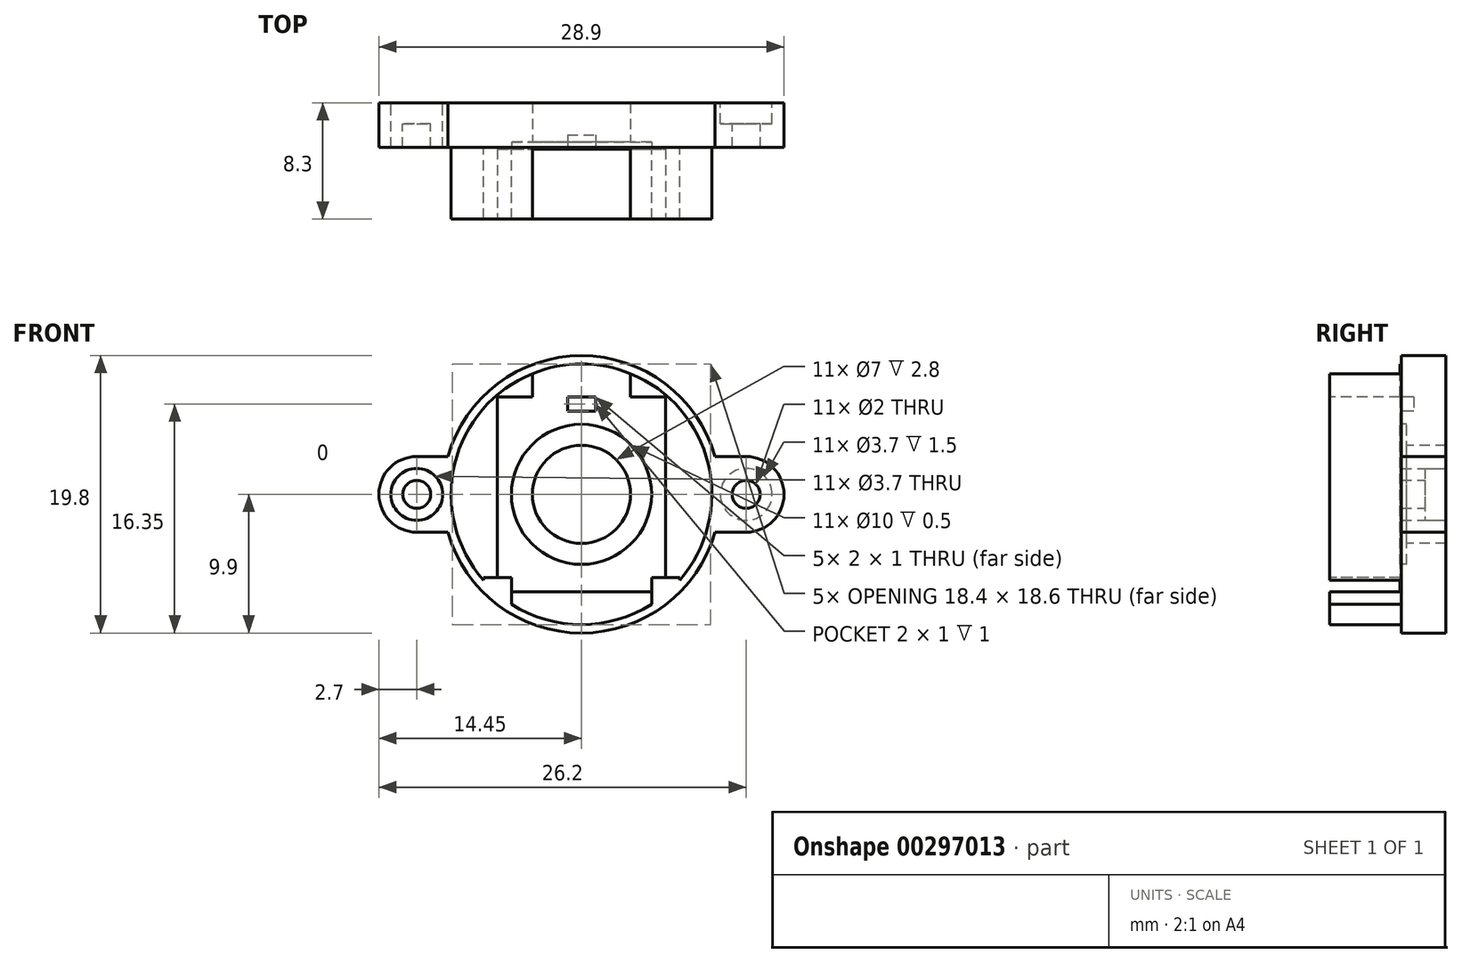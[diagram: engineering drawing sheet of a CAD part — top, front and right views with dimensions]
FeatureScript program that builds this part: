
annotation { "Feature Type Name" : "Feature", "Feature Type Description" : "" }
export const myFeature = defineFeature(function(context is Context, id is Id, definition is map)
    precondition{}
    {
        {
            var Q0;
            Q0=qCreatedBy(makeId("Top.planeOp"),FACE);
            var sketch = newSketch(context, id + "F0", { "sketchPlane" : qUnion([Q0])});
            skLineSegment(sketch, "E0", {"start": v(0, -5.1) * mm, "end": v(-9.3, -5.1) * mm});
            skLineSegment(sketch, "E1", {"start": v(-9.3, -5.1) * mm, "end": v(-9.3, 0) * mm});
            skLineSegment(sketch, "E2", {"start": v(-9.3, 0) * mm, "end": v(-9.9, 0) * mm});
            skLineSegment(sketch, "E3", {"start": v(-9.9, 0) * mm, "end": v(-9.9, 3.2) * mm});
            skLineSegment(sketch, "E4", {"start": v(-9.9, 3.2) * mm, "end": v(0, 3.2) * mm});
            skLineSegment(sketch, "E5", {"start": v(0, 3.2) * mm, "end": v(0, -5.1) * mm});
            skSolve(sketch);
        }
        {
            var Q0;
            Q0=makeQuery(id+"F0.imprint","IMPRINT",FACE,{"disambiguationData":[TD([[makeQuery(id+"F0.imprint","IMPRINT",EDGE,{"derivedFrom":sQuery(id+"F0.wireOp",EDGE,"E0")}),-1.0]])]});
            var Q1;
            Q1=sQuery(id+"F0.wireOp",EDGE,"E5");
            revolve(context, id + "F1", {"entities" : qUnion([Q0]), "axis" : qUnion([Q1]), "revolveType" : RevolveType.FULL});
        }
        {
            var Q0;
            Q0=makeQuery(id+"F1.opRevolve","SWEPT_FACE",FACE,{"disambiguationData":[OSD([sQuery(id+"F0.wireOp",EDGE,"E4")])]});
            var sketch = newSketch(context, id + "F2", { "sketchPlane" : qUnion([Q0])});
            skLineSegment(sketch, "E6", {"start": v(9.52, -2.7) * mm, "end": v(11.75, -2.7) * mm});
            skArc(sketch, "E7", {"start": v(11.75, -2.7) * mm, "mid": v(13.66, -1.9) * mm, "end": v(14.45, 0) * mm});
            skPoint(sketch, "E8", {"position": v(14.45, 0) * mm});
            skPoint(sketch, "E8.positionSnap0", {"position": v(14.45, 0) * mm});
            skPoint(sketch, "E9", {"position": v(9.9, 0) * mm});
            skLineSegment(sketch, "E10", {"start": v(0, -2.12) * mm, "end": v(0, 2.3) * mm, "construction": true});
            skLineSegment(sketch, "E11.MirrorCS", {"start": v(-9.52, -2.7) * mm, "end": v(-11.75, -2.7) * mm});
            skArc(sketch, "E12.MirrorCS", {"start": v(-11.75, -2.7) * mm, "mid": v(-13.66, -1.9) * mm, "end": v(-14.45, 0) * mm});
            skPoint(sketch, "E13.MirrorP", {"position": v(-14.45, 0) * mm});
            skPoint(sketch, "E14.end.orphan", {"position": v(9.52, 2.7) * mm});
            skPoint(sketch, "E14.start.orphan", {"position": v(11.75, 2.7) * mm});
            skPoint(sketch, "E15.MirrorCS.end.orphan", {"position": v(-9.52, 2.7) * mm});
            skPoint(sketch, "E15.MirrorCS.start.orphan", {"position": v(-11.75, 2.7) * mm});
            skLineSegment(sketch, "E16", {"start": v(2.14, 0) * mm, "end": v(-2.79, 0) * mm, "construction": true});
            skArc(sketch, "E17.MirrorCS", {"start": v(11.75, 2.7) * mm, "mid": v(13.66, 1.9) * mm, "end": v(14.45, 0) * mm});
            skLineSegment(sketch, "E18.MirrorCS", {"start": v(9.52, 2.7) * mm, "end": v(11.75, 2.7) * mm});
            skLineSegment(sketch, "E19.MirrorCS", {"start": v(-9.52, 2.7) * mm, "end": v(-11.75, 2.7) * mm});
            skArc(sketch, "E20.MirrorCS", {"start": v(-11.75, 2.7) * mm, "mid": v(-13.66, 1.9) * mm, "end": v(-14.45, 0) * mm});
            skPoint(sketch, "E21", {"position": v(-9.9, 0) * mm});
            skArc(sketch, "E22", {"start": v(9.52, -2.7) * mm, "mid": v(9.9, 0) * mm, "end": v(9.52, 2.7) * mm});
            skArc(sketch, "E23.MirrorCS", {"start": v(-9.52, -2.7) * mm, "mid": v(-9.9, 0) * mm, "end": v(-9.52, 2.7) * mm});
            skCircle(sketch, "E24", {"center": v(-11.75, 0) * mm, "radius": 1 * mm});
            skCircle(sketch, "E25.MirrorC", {"center": v(11.75, 0) * mm, "radius": 1 * mm});
            skPoint(sketch, "E26", {"position": v(10.75, 0) * mm});
            skPoint(sketch, "E27", {"position": v(-10.75, 0) * mm});
            skCircle(sketch, "E28", {"center": v(11.75, 0) * mm, "radius": 1.85 * mm});
            skCircle(sketch, "E29.MirrorC", {"center": v(-11.75, 0) * mm, "radius": 1.85 * mm});
            skSolve(sketch);
        }
        {
            var Q0;
            Q0=makeQuery(id+"F2.imprint","IMPRINT",FACE,{"disambiguationData":[TD([[makeQuery(id+"F2.imprint","IMPRINT",EDGE,{"derivedFrom":sQuery(id+"F2.wireOp",EDGE,"E11.MirrorCS")}),-1.0]])]});
            var Q1;
            Q1=makeQuery(id+"F2.imprint","IMPRINT",FACE,{"disambiguationData":[TD([[makeQuery(id+"F2.imprint","IMPRINT",EDGE,{"derivedFrom":sQuery(id+"F2.wireOp",EDGE,"E11.MirrorCS")}),-1.0]])]});
            var Q2;
            Q2=makeQuery(id+"F2.imprint","IMPRINT",FACE,{"disambiguationData":[TD([[makeQuery(id+"F2.imprint","IMPRINT",EDGE,{"derivedFrom":sQuery(id+"F2.wireOp",EDGE,"E11.MirrorCS")}),-1.0]])]});
            var Q3;
            Q3=makeQuery(id+"F2.imprint","IMPRINT",FACE,{"disambiguationData":[TD([[makeQuery(id+"F2.imprint","IMPRINT",EDGE,{"derivedFrom":sQuery(id+"F2.wireOp",EDGE,"E24")}),-1.0]])]});
            extrude(context, id + "F3", {"entities" : qUnion([Q0, Q1, Q2, Q3]), "oppositeDirection" : true, "depth" : 3.2 * mm});
        }
        {
            var Q0;
            Q0=makeQuery(id+"F1.opRevolve","SWEPT_FACE",FACE,{"disambiguationData":[OSD([sQuery(id+"F0.wireOp",EDGE,"E0")])]});
            var sketch = newSketch(context, id + "F4", { "sketchPlane" : qUnion([Q0])});
            skLineSegment(sketch, "E30.bottom", {"start": v(-6, 6.95) * mm, "end": v(6, 6.95) * mm});
            skLineSegment(sketch, "E30.top", {"start": v(-6, -6.95) * mm, "end": v(6, -6.95) * mm});
            skLineSegment(sketch, "E30.left", {"start": v(-6, 6.95) * mm, "end": v(-6, -6.95) * mm});
            skLineSegment(sketch, "E30.right", {"start": v(6, 6.95) * mm, "end": v(6, -6.95) * mm});
            skPoint(sketch, "E30.middle", {"position": v(0, 0) * mm});
            skSolve(sketch);
        }
        {
            var Q0;
            Q0 = qSketchRegion(id + "F4", true);
            extrude(context, id + "F5", {"entities" : qUnion([Q0]), "operationType" : NewBodyOperationType.REMOVE, "oppositeDirection" : true, "depth" : 5 * mm});
        }
        {
            var Q0;
            Q0=sQuery(id+"F4.wireOp",VERTEX,"E30.middle");
            var Q1;
            Q1=makeQuery(id+"F1.opRevolve","SWEPT_BODY",BODY,{"disambiguationData":[OSD([sQuery(id+"F0.wireOp",EDGE,"E0"),sQuery(id+"F0.wireOp",EDGE,"E1"),sQuery(id+"F0.wireOp",EDGE,"E2"),sQuery(id+"F0.wireOp",EDGE,"E3"),sQuery(id+"F0.wireOp",EDGE,"E4"),sQuery(id+"F0.wireOp",EDGE,"E5")])]});
            hole(context, id + "F6", {"style" : HoleStyle.SIMPLE, "endStyle" : HoleEndStyle.THROUGH, "holeDiameter" : 7 * mm, "tappedDepth" : 12 * mm, "tapClearance" : 3, "locations" : qUnion([Q0]), "scope" : qUnion([Q1])});
        }
        {
            var Q0;
            Q0=makeQuery(id+"F4.imprint","IMPRINT",FACE,{"disambiguationData":[TD([[makeQuery(id+"F4.imprint","IMPRINT",EDGE,{"derivedFrom":sQuery(id+"F4.wireOp",EDGE,"E30.bottom")}),1.0]])]});
            var sketch = newSketch(context, id + "F7", { "sketchPlane" : qUnion([Q0])});
            skLineSegment(sketch, "E31.bottom", {"start": v(1, 6.95) * mm, "end": v(-1, 6.95) * mm});
            skLineSegment(sketch, "E31.top", {"start": v(1, 5.95) * mm, "end": v(-1, 5.95) * mm});
            skLineSegment(sketch, "E31.left", {"start": v(1, 6.95) * mm, "end": v(1, 5.95) * mm});
            skLineSegment(sketch, "E31.right", {"start": v(-1, 6.95) * mm, "end": v(-1, 5.95) * mm});
            skPoint(sketch, "E32", {"position": v(0, 6.95) * mm});
            skSolve(sketch);
        }
        {
            var Q0;
            Q0 = qSketchRegion(id + "F7", true);
            extrude(context, id + "F8", {"entities" : qUnion([Q0]), "operationType" : NewBodyOperationType.REMOVE, "oppositeDirection" : true, "depth" : 6 * mm});
        }
        {
            var Q0;
            Q0=makeQuery(id+"F4.imprint","IMPRINT",FACE,{"disambiguationData":[TD([[makeQuery(id+"F4.imprint","IMPRINT",EDGE,{"derivedFrom":sQuery(id+"F4.wireOp",EDGE,"E30.bottom")}),1.0]])]});
            var sketch = newSketch(context, id + "F9", { "sketchPlane" : qUnion([Q0])});
            skLineSegment(sketch, "E33.bottom", {"start": v(-3.5, 6.95) * mm, "end": v(3.5, 6.95) * mm});
            skLineSegment(sketch, "E33.top", {"start": v(-3.5, 16.95) * mm, "end": v(3.5, 16.95) * mm});
            skLineSegment(sketch, "E33.left", {"start": v(-3.5, 6.95) * mm, "end": v(-3.5, 16.95) * mm});
            skLineSegment(sketch, "E33.right", {"start": v(3.5, 6.95) * mm, "end": v(3.5, 16.95) * mm});
            skPoint(sketch, "E34", {"position": v(0, 6.95) * mm});
            skSolve(sketch);
        }
        {
            var Q0;
            Q0 = qSketchRegion(id + "F9", true);
            extrude(context, id + "F10", {"entities" : qUnion([Q0]), "operationType" : NewBodyOperationType.REMOVE, "oppositeDirection" : true, "depth" : 5 * mm});
        }
        {
            var Q0;
            {var subQ1=sQuery(id+"F2.wireOp",EDGE,"E6");Q0=makeQuery(id+"F2.imprint","IMPRINT",FACE,{"disambiguationData":[TD([[makeQuery(id+"F2.imprint","IMPRINT",EDGE,{"derivedFrom":subQ1}),1.0]])]});}
            var Q1;
            Q1=makeQuery(id+"F2.imprint","IMPRINT",FACE,{"disambiguationData":[TD([[makeQuery(id+"F2.imprint","IMPRINT",EDGE,{"derivedFrom":sQuery(id+"F2.wireOp",EDGE,"E25.MirrorC")}),1.0]])]});
            var Q2;
            Q2=makeQuery(id+"F2.imprint","IMPRINT",FACE,{"disambiguationData":[TD([[makeQuery(id+"F2.imprint","IMPRINT",EDGE,{"derivedFrom":sQuery(id+"F2.wireOp",EDGE,"E25.MirrorC")}),-1.0]])]});
            extrude(context, id + "F11", {"entities" : qUnion([Q0, Q1, Q2]), "oppositeDirection" : true, "depth" : 3.2 * mm});
        }
        {
            var Q0;
            Q0=makeQuery(id+"F3.opExtrude","SWEPT_BODY",BODY,{"disambiguationData":[OSD([sQuery(id+"F2.wireOp",EDGE,"E11.MirrorCS"),sQuery(id+"F2.wireOp",EDGE,"E12.MirrorCS"),sQuery(id+"F2.wireOp",EDGE,"E19.MirrorCS"),sQuery(id+"F2.wireOp",EDGE,"E20.MirrorCS"),sQuery(id+"F2.wireOp",EDGE,"E23.MirrorCS")])]});
            var Q1;
            Q1=makeQuery(id+"F11.opExtrude","SWEPT_BODY",BODY,{"disambiguationData":[OSD([sQuery(id+"F2.wireOp",EDGE,"E6"),sQuery(id+"F2.wireOp",EDGE,"E7"),sQuery(id+"F2.wireOp",EDGE,"E17.MirrorCS"),sQuery(id+"F2.wireOp",EDGE,"E18.MirrorCS"),sQuery(id+"F2.wireOp",EDGE,"E22")])]});
            var Q2;
            Q2=makeQuery(id+"F1.opRevolve","SWEPT_BODY",BODY,{"disambiguationData":[OSD([sQuery(id+"F0.wireOp",EDGE,"E0"),sQuery(id+"F0.wireOp",EDGE,"E1"),sQuery(id+"F0.wireOp",EDGE,"E2"),sQuery(id+"F0.wireOp",EDGE,"E3"),sQuery(id+"F0.wireOp",EDGE,"E4"),sQuery(id+"F0.wireOp",EDGE,"E5")])]});
            booleanBodies(context, id + "F12", {"operationType" : BooleanOperationType.UNION, "tools" : qUnion([Q0, Q1, Q2])});
        }
        {
            var Q0;
            Q0=makeQuery(id+"F2.imprint","IMPRINT",FACE,{"disambiguationData":[TD([[makeQuery(id+"F2.imprint","IMPRINT",EDGE,{"derivedFrom":sQuery(id+"F2.wireOp",EDGE,"E25.MirrorC")}),1.0]])]});
            var Q1;
            Q1=makeQuery(id+"F2.imprint","IMPRINT",FACE,{"disambiguationData":[TD([[makeQuery(id+"F2.imprint","IMPRINT",EDGE,{"derivedFrom":sQuery(id+"F2.wireOp",EDGE,"E24")}),-1.0]])]});
            extrude(context, id + "F13", {"entities" : qUnion([Q0, Q1]), "operationType" : NewBodyOperationType.REMOVE, "oppositeDirection" : true, "depth" : 1.5 * mm});
        }
        {
            var Q0;
            Q0=makeQuery(id+"F2.imprint","IMPRINT",FACE,{"disambiguationData":[TD([[makeQuery(id+"F2.imprint","IMPRINT",EDGE,{"derivedFrom":sQuery(id+"F2.wireOp",EDGE,"E25.MirrorC")}),-1.0]])]});
            extrude(context, id + "F14", {"entities" : qUnion([Q0]), "operationType" : NewBodyOperationType.REMOVE, "oppositeDirection" : true, "depth" : 25 * mm});
        }
        {
            var Q0;
            Q0=makeQuery(id+"F10.boolean.opBoolean","MERGE",FACE,{"derivedFrom":[makeQuery(id+"F5.boolean.opBoolean","COPY",FACE,{"derivedFrom":makeQuery(id+"F5.opExtrude","CAP_FACE",FACE,{"disambiguationData":[OSD([sQuery(id+"F4.wireOp",EDGE,"E30.bottom"),sQuery(id+"F4.wireOp",EDGE,"E30.top"),sQuery(id+"F4.wireOp",EDGE,"E30.left"),sQuery(id+"F4.wireOp",EDGE,"E30.right")])],"isStart":false})}),makeQuery(id+"F10.opExtrude","CAP_FACE",FACE,{"disambiguationData":[OSD([sQuery(id+"F9.wireOp",EDGE,"E33.bottom"),sQuery(id+"F9.wireOp",EDGE,"E33.top"),sQuery(id+"F9.wireOp",EDGE,"E33.left"),sQuery(id+"F9.wireOp",EDGE,"E33.right")])],"isStart":false})]});
            var sketch = newSketch(context, id + "F15", { "sketchPlane" : qUnion([Q0])});
            skCircle(sketch, "E35", {"center": v(0, 0) * mm, "radius": 5 * mm});
            skSolve(sketch);
        }
        {
            var Q0;
            Q0 = qSketchRegion(id + "F15", true);
            extrude(context, id + "F16", {"entities" : qUnion([Q0]), "operationType" : NewBodyOperationType.REMOVE, "oppositeDirection" : true, "depth" : .5 * mm});
        }
        {
            var Q0;
            Q0=makeQuery(id+"F4.imprint","IMPRINT",FACE,{"disambiguationData":[TD([[makeQuery(id+"F4.imprint","IMPRINT",EDGE,{"derivedFrom":sQuery(id+"F4.wireOp",EDGE,"E30.bottom")}),1.0]])]});
            var sketch = newSketch(context, id + "F17", { "sketchPlane" : qUnion([Q0])});
            skLineSegment(sketch, "E36.bottom", {"start": v(-5, -5.95) * mm, "end": v(-7, -5.95) * mm});
            skLineSegment(sketch, "E36.top", {"start": v(-5, -7.95) * mm, "end": v(-7, -7.95) * mm});
            skLineSegment(sketch, "E36.left", {"start": v(-5, -5.95) * mm, "end": v(-5, -7.95) * mm});
            skLineSegment(sketch, "E36.right", {"start": v(-7, -5.95) * mm, "end": v(-7, -7.95) * mm});
            skPoint(sketch, "E36.middle", {"position": v(-6, -6.95) * mm});
            skLineSegment(sketch, "E37.bottom", {"start": v(5, -5.95) * mm, "end": v(7, -5.95) * mm});
            skLineSegment(sketch, "E37.top", {"start": v(5, -7.95) * mm, "end": v(7, -7.95) * mm});
            skLineSegment(sketch, "E37.left", {"start": v(5, -5.95) * mm, "end": v(5, -7.95) * mm});
            skLineSegment(sketch, "E37.right", {"start": v(7, -5.95) * mm, "end": v(7, -7.95) * mm});
            skPoint(sketch, "E37.middle", {"position": v(6, -6.95) * mm});
            skSolve(sketch);
        }
        {
            var Q0;
            Q0 = qSketchRegion(id + "F17", true);
            var Q1;
            Q1=makeQuery(id+"F12.opBoolean","MERGE",FACE,{"derivedFrom":[makeQuery(id+"F1.opRevolve","SWEPT_FACE",FACE,{"disambiguationData":[OSD([sQuery(id+"F0.wireOp",EDGE,"E2")])]}),makeQuery(id+"F3.opExtrude","CAP_FACE",FACE,{"disambiguationData":[OSD([sQuery(id+"F2.wireOp",EDGE,"E11.MirrorCS"),sQuery(id+"F2.wireOp",EDGE,"E12.MirrorCS"),sQuery(id+"F2.wireOp",EDGE,"E19.MirrorCS"),sQuery(id+"F2.wireOp",EDGE,"E20.MirrorCS"),sQuery(id+"F2.wireOp",EDGE,"E23.MirrorCS"),sQuery(id+"F2.wireOp",EDGE,"E24")])],"isStart":false}),makeQuery(id+"F11.opExtrude","CAP_FACE",FACE,{"disambiguationData":[OSD([sQuery(id+"F2.wireOp",EDGE,"E6"),sQuery(id+"F2.wireOp",EDGE,"E7"),sQuery(id+"F2.wireOp",EDGE,"E17.MirrorCS"),sQuery(id+"F2.wireOp",EDGE,"E18.MirrorCS"),sQuery(id+"F2.wireOp",EDGE,"E22")])],"isStart":false})]});
            extrude(context, id + "F18", {"entities" : qUnion([Q0]), "operationType" : NewBodyOperationType.REMOVE, "endBound" : BoundingType.UP_TO_SURFACE, "oppositeDirection" : true, "endBoundEntityFace" : qUnion([Q1]), "depth" : 25 * mm});
        }
    });
